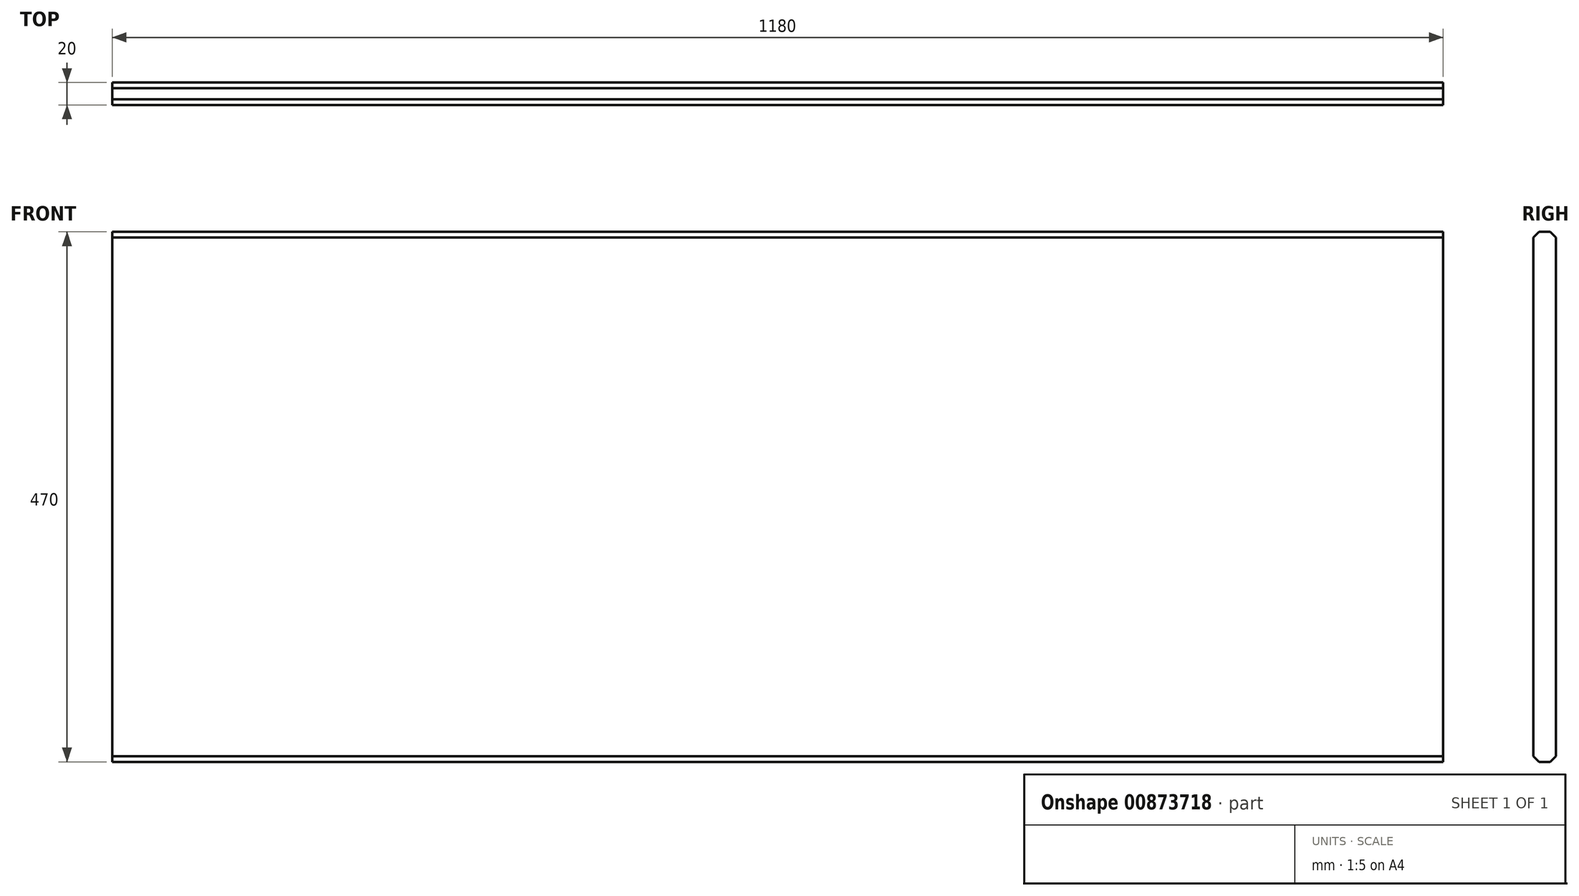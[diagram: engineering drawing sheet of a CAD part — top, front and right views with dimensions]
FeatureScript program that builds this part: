
annotation { "Feature Type Name" : "Feature", "Feature Type Description" : "" }
export const myFeature = defineFeature(function(context is Context, id is Id, definition is map)
    precondition{}
    {
        {
            var Q0;
            Q0=qCreatedBy(makeId("Front.planeOp"),FACE);
            var sketch = newSketch(context, id + "F0", { "sketchPlane" : qUnion([Q0])});
            skLineSegment(sketch, "E0.bottom", {"start": v(0, 0) * mm, "end": v(1180, 0) * mm});
            skLineSegment(sketch, "E0.top", {"start": v(0, 470) * mm, "end": v(1180, 470) * mm});
            skLineSegment(sketch, "E0.left", {"start": v(0, 0) * mm, "end": v(0, 470) * mm});
            skLineSegment(sketch, "E0.right", {"start": v(1180, 0) * mm, "end": v(1180, 470) * mm});
            skSolve(sketch);
        }
        {
            var Q0;
            Q0 = qSketchRegion(id + "F0", true);
            extrude(context, id + "F1", {"entities" : qUnion([Q0]), "depth" : 20 * mm, "offsetDistance" : 25 * mm});
        }
        {
            var Q0;
            Q0=makeQuery(id+"F1.opExtrude","CAP_EDGE",EDGE,{"disambiguationData":[OSD([sQuery(id+"F0.wireOp",EDGE,"E0.bottom")])],"isStart":false});
            var Q1;
            Q1=makeQuery(id+"F1.opExtrude","CAP_EDGE",EDGE,{"disambiguationData":[OSD([sQuery(id+"F0.wireOp",EDGE,"E0.bottom")])],"isStart":true});
            var Q2;
            Q2=makeQuery(id+"F1.opExtrude","CAP_EDGE",EDGE,{"disambiguationData":[OSD([sQuery(id+"F0.wireOp",EDGE,"E0.top")])],"isStart":false});
            var Q3;
            Q3=makeQuery(id+"F1.opExtrude","CAP_EDGE",EDGE,{"disambiguationData":[OSD([sQuery(id+"F0.wireOp",EDGE,"E0.top")])],"isStart":true});
            chamfer(context, id + "F2", {"entities" : qUnion([Q0, Q1, Q2, Q3]), "width" : 5 * mm, "tangentPropagation" : true});
        }
    });
